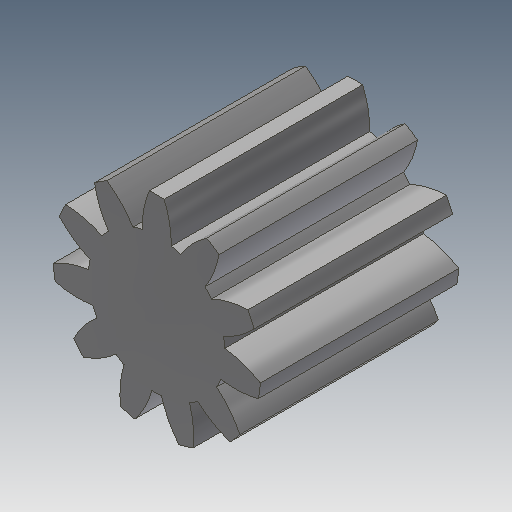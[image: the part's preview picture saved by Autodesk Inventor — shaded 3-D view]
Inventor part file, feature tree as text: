
AUTODESK INVENTOR PART (.ipt)
format: ipt  version: 2017 (Build 210142000, 142)  size: 205,824 bytes
history: native  units: mm (DEFAULTED — no unit token found)
features: plane x3, other x3, sketch x2, extrude x1
ambient origin geometry x8: Origin, YZ Plane, XZ Plane, XY Plane, X Axis, Y Axis, Z Axis, Center Point
bodies: Solid1 (feature_tree)
feature tree (9):
  extrude  "Extrusion1"  Depth=2.5mm TaperAngle=0.0deg
  plane  "Work Plane2"
  plane  "Work Plane8"
  plane  "Work Plane9"
  other  "Цилиндрическое зубчатое зацепление"
  sketch  "Sketch1"  dims[d0=2.615713mm d1=2.5mm d2=0.0mm]
  sketch  "Sketch2"  dims[d3=2.218098mm d4=10.0mm d5=0.0mm d16=5.948535mm d17=0.0mm d34=2.855993mm d39=0.0mm d41=0.0mm d43=5.948535mm d46=5.948535mm d47=0.0mm d48=0.0mm]
  other  "Srf1"
  other  "Средний диаметр"
